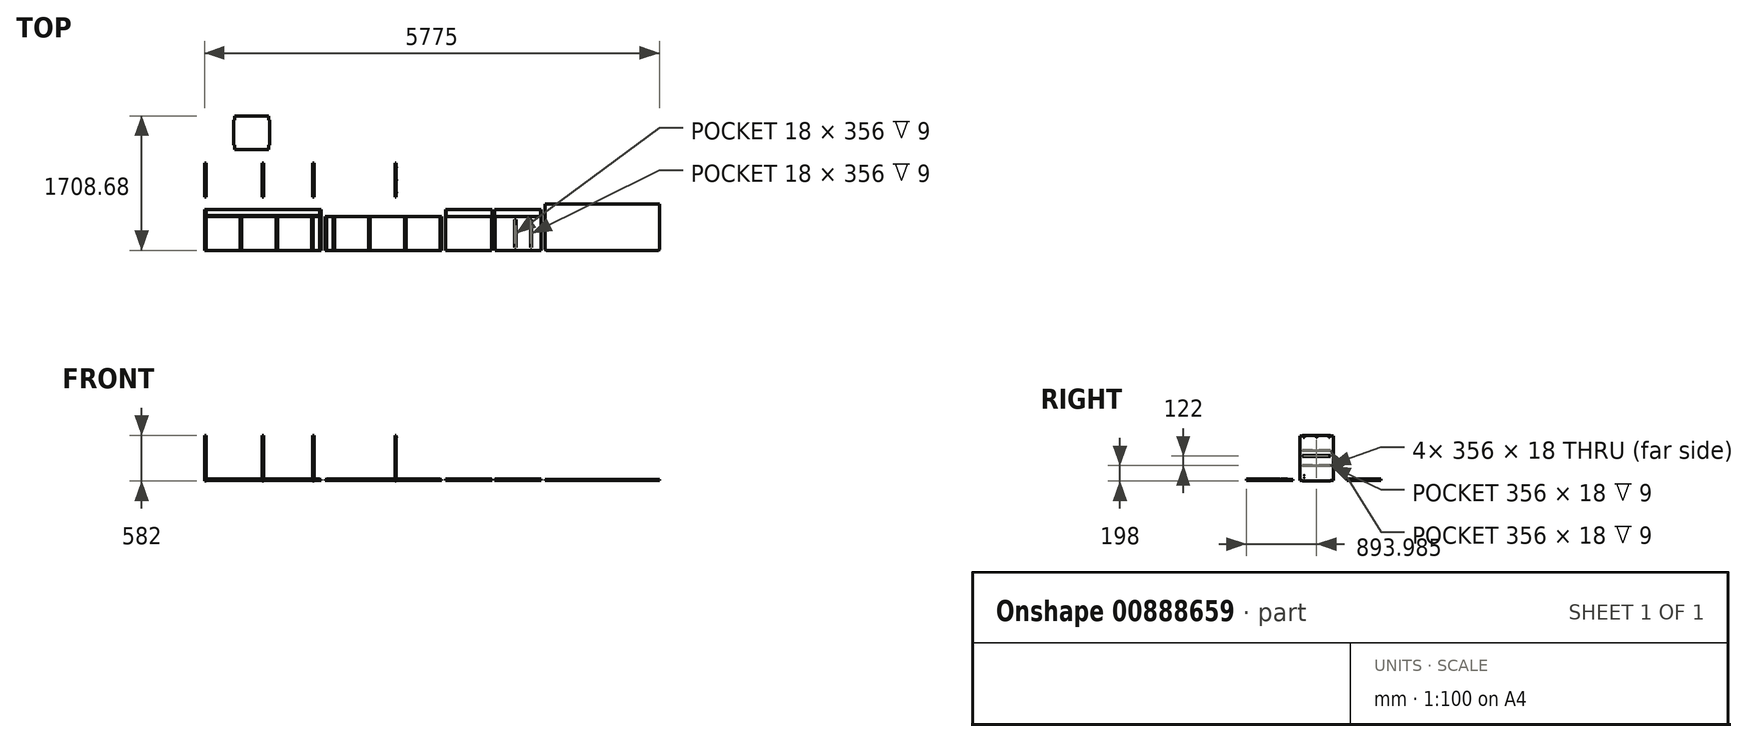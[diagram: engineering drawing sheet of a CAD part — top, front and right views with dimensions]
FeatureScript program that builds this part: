
annotation { "Feature Type Name" : "Feature", "Feature Type Description" : "" }
export const myFeature = defineFeature(function(context is Context, id is Id, definition is map)
    precondition{}
    {
        {
            assignVariable(context, id + "F0", {"name" : "ply", "anyValue" : 18});
        }
        {
            assignVariable(context, id + "F1", {"name" : "back_ply", "anyValue" : 12});
        }
        {
            assignVariable(context, id + "F2", {"name" : "cutter_rad", "anyValue" : 5});
        }
        {
            var Q0;
            Q0=qCreatedBy(makeId("Top.planeOp"),FACE);
            var sketch = newSketch(context, id + "F3", { "sketchPlane" : qUnion([Q0])});
            skLineSegment(sketch, "E0.bottom", {"start": v(0, 0) * mm, "end": v(1480, 0) * mm});
            skLineSegment(sketch, "E0.top", {"start": v(0, 520) * mm, "end": v(1480, 520) * mm});
            skLineSegment(sketch, "E0.left", {"start": v(0, 0) * mm, "end": v(0, 520) * mm});
            skLineSegment(sketch, "E0.right", {"start": v(1480, 0) * mm, "end": v(1480, 520) * mm});
            skSolve(sketch);
        }
        {
            var Q0;
            Q0=makeQuery(id+"F3.imprint","IMPRINT",FACE,{"disambiguationData":[TD([[makeQuery(id+"F3.imprint","IMPRINT",EDGE,{"derivedFrom":sQuery(id+"F3.wireOp",EDGE,"E0.bottom")}),1.0]])]});
            extrude(context, id + "F4", {"entities" : qUnion([Q0]), "depth" : (getVariable(context, 'ply')) * mm, "offsetDistance" : 25 * mm});
        }
        {
            var Q0;
            Q0=makeQuery(id+"F4.opExtrude","CAP_FACE",FACE,{"disambiguationData":[OSD([sQuery(id+"F3.wireOp",EDGE,"E0.bottom"),sQuery(id+"F3.wireOp",EDGE,"E0.top"),sQuery(id+"F3.wireOp",EDGE,"E0.left"),sQuery(id+"F3.wireOp",EDGE,"E0.right")])],"isStart":false});
            var sketch = newSketch(context, id + "F5", { "sketchPlane" : qUnion([Q0])});
            skLineSegment(sketch, "E1.bottom", {"start": v(14, 428) * mm, "end": v(1466, 428) * mm});
            skLineSegment(sketch, "E1.top", {"start": v(14, 440.5) * mm, "end": v(1466, 440.5) * mm});
            skLineSegment(sketch, "E1.left", {"start": v(9, 433) * mm, "end": v(9, 435.5) * mm});
            skLineSegment(sketch, "E1.right", {"start": v(1471, 433) * mm, "end": v(1471, 435.5) * mm});
            skPoint(sketch, "E2.visualSharp", {"position": v(9, 440.5) * mm});
            skArc(sketch, "E2.filletArc", {"start": v(14, 440.5) * mm, "mid": v(10.46, 439.04) * mm, "end": v(9, 435.5) * mm});
            skPoint(sketch, "E3.visualSharp", {"position": v(9, 428) * mm});
            skArc(sketch, "E3.filletArc", {"start": v(9, 433) * mm, "mid": v(10.46, 429.46) * mm, "end": v(14, 428) * mm});
            skPoint(sketch, "E4.visualSharp", {"position": v(1471, 440.5) * mm});
            skArc(sketch, "E4.filletArc", {"start": v(1471, 435.5) * mm, "mid": v(1469.54, 439.04) * mm, "end": v(1466, 440.5) * mm});
            skPoint(sketch, "E5.visualSharp", {"position": v(1471, 428) * mm});
            skArc(sketch, "E5.filletArc", {"start": v(1466, 428) * mm, "mid": v(1469.54, 429.46) * mm, "end": v(1471, 433) * mm});
            skLineSegment(sketch, "E6.bottom", {"start": v(0, 0) * mm, "end": v(18, 0) * mm});
            skLineSegment(sketch, "E6.top", {"start": v(0, 520) * mm, "end": v(18, 520) * mm});
            skLineSegment(sketch, "E6.left", {"start": v(0, 0) * mm, "end": v(0, 520) * mm});
            skLineSegment(sketch, "E6.right", {"start": v(18, 0) * mm, "end": v(18, 520) * mm});
            skLineSegment(sketch, "E7", {"start": v(740, 520) * mm, "end": v(740, 0) * mm, "construction": true});
            skLineSegment(sketch, "E8.MirrorCS", {"start": v(1462, 0) * mm, "end": v(1462, 520) * mm});
            skLineSegment(sketch, "E9.MirrorCS", {"start": v(1480, 520) * mm, "end": v(1462, 520) * mm});
            skLineSegment(sketch, "E10.MirrorCS", {"start": v(1480, 0) * mm, "end": v(1480, 520) * mm});
            skLineSegment(sketch, "E11.MirrorCS", {"start": v(1480, 0) * mm, "end": v(1462, 0) * mm});
            skLineSegment(sketch, "E12.bottom", {"start": v(458.33, 18) * mm, "end": v(466.33, 18) * mm});
            skLineSegment(sketch, "E12.top", {"start": v(458.33, 410) * mm, "end": v(466.33, 410) * mm});
            skLineSegment(sketch, "E12.left", {"start": v(453.33, 23) * mm, "end": v(453.33, 405) * mm});
            skLineSegment(sketch, "E12.right", {"start": v(471.33, 23) * mm, "end": v(471.33, 405) * mm});
            skPoint(sketch, "E13.visualSharp", {"position": v(453.33, 410) * mm});
            skArc(sketch, "E13.filletArc", {"start": v(458.33, 410) * mm, "mid": v(454.8, 408.54) * mm, "end": v(453.33, 405) * mm});
            skPoint(sketch, "E14.visualSharp", {"position": v(471.33, 410) * mm});
            skArc(sketch, "E14.filletArc", {"start": v(471.33, 405) * mm, "mid": v(469.87, 408.54) * mm, "end": v(466.33, 410) * mm});
            skPoint(sketch, "E15.visualSharp", {"position": v(453.33, 18) * mm});
            skArc(sketch, "E15.filletArc", {"start": v(453.33, 23) * mm, "mid": v(454.8, 19.46) * mm, "end": v(458.33, 18) * mm});
            skPoint(sketch, "E16.visualSharp", {"position": v(471.33, 18) * mm});
            skArc(sketch, "E16.filletArc", {"start": v(466.33, 18) * mm, "mid": v(469.87, 19.46) * mm, "end": v(471.33, 23) * mm});
            skLineSegment(sketch, "E17.bottom", {"start": v(911.67, 18) * mm, "end": v(919.67, 18) * mm});
            skLineSegment(sketch, "E17.top", {"start": v(911.67, 410) * mm, "end": v(919.67, 410) * mm});
            skLineSegment(sketch, "E17.left", {"start": v(906.67, 23) * mm, "end": v(906.67, 405) * mm});
            skLineSegment(sketch, "E17.right", {"start": v(924.67, 23) * mm, "end": v(924.67, 405) * mm});
            skPoint(sketch, "E18.visualSharp", {"position": v(906.67, 410) * mm});
            skArc(sketch, "E18.filletArc", {"start": v(911.67, 410) * mm, "mid": v(908.13, 408.54) * mm, "end": v(906.67, 405) * mm});
            skPoint(sketch, "E19.visualSharp", {"position": v(924.67, 410) * mm});
            skArc(sketch, "E19.filletArc", {"start": v(924.67, 405) * mm, "mid": v(923.2, 408.54) * mm, "end": v(919.67, 410) * mm});
            skPoint(sketch, "E20.visualSharp", {"position": v(906.67, 18) * mm});
            skArc(sketch, "E20.filletArc", {"start": v(906.67, 23) * mm, "mid": v(908.13, 19.46) * mm, "end": v(911.67, 18) * mm});
            skPoint(sketch, "E21.visualSharp", {"position": v(924.67, 18) * mm});
            skArc(sketch, "E21.filletArc", {"start": v(919.67, 18) * mm, "mid": v(923.2, 19.46) * mm, "end": v(924.67, 23) * mm});
            skLineSegment(sketch, "E22.bottom", {"start": v(1365, 18) * mm, "end": v(1373, 18) * mm});
            skLineSegment(sketch, "E22.top", {"start": v(1365, 410) * mm, "end": v(1373, 410) * mm});
            skLineSegment(sketch, "E22.left", {"start": v(1360, 23) * mm, "end": v(1360, 405) * mm});
            skLineSegment(sketch, "E22.right", {"start": v(1378, 23) * mm, "end": v(1378, 405) * mm});
            skPoint(sketch, "E23.visualSharp", {"position": v(1360, 410) * mm});
            skArc(sketch, "E23.filletArc", {"start": v(1365, 410) * mm, "mid": v(1361.46, 408.54) * mm, "end": v(1360, 405) * mm});
            skPoint(sketch, "E24.visualSharp", {"position": v(1378, 410) * mm});
            skArc(sketch, "E24.filletArc", {"start": v(1378, 405) * mm, "mid": v(1376.54, 408.54) * mm, "end": v(1373, 410) * mm});
            skPoint(sketch, "E25.visualSharp", {"position": v(1360, 18) * mm});
            skArc(sketch, "E25.filletArc", {"start": v(1360, 23) * mm, "mid": v(1361.46, 19.46) * mm, "end": v(1365, 18) * mm});
            skPoint(sketch, "E26.visualSharp", {"position": v(1378, 18) * mm});
            skArc(sketch, "E26.filletArc", {"start": v(1373, 18) * mm, "mid": v(1376.54, 19.46) * mm, "end": v(1378, 23) * mm});
            skSolve(sketch);
        }
        {
            var Q0;
            Q0 = qSketchRegion(id + "F5", true);
            extrude(context, id + "F6", {"entities" : qUnion([Q0]), "operationType" : NewBodyOperationType.REMOVE, "oppositeDirection" : true, "depth" : (getVariable(context, 'ply') / 2) * mm, "offsetDistance" : 25 * mm});
        }
        {
            var Q0;
            Q0=qCreatedBy(makeId("Top.planeOp"),FACE);
            var sketch = newSketch(context, id + "F7", { "sketchPlane" : qUnion([Q0])});
            skLineSegment(sketch, "E27.bottom", {"start": v(1530, 0) * mm, "end": v(3010, 0) * mm});
            skLineSegment(sketch, "E27.top", {"start": v(1530, 428) * mm, "end": v(3010, 428) * mm});
            skLineSegment(sketch, "E27.left", {"start": v(1530, 0) * mm, "end": v(1530, 428) * mm});
            skLineSegment(sketch, "E27.right", {"start": v(3010, 0) * mm, "end": v(3010, 428) * mm});
            skSolve(sketch);
        }
        {
            var Q0;
            Q0 = qSketchRegion(id + "F7", true);
            extrude(context, id + "F8", {"entities" : qUnion([Q0]), "depth" : (getVariable(context, 'ply')) * mm, "offsetDistance" : 25 * mm});
        }
        {
            var Q0;
            Q0=makeQuery(id+"F8.opExtrude","CAP_FACE",FACE,{"disambiguationData":[OSD([sQuery(id+"F7.wireOp",EDGE,"E27.bottom"),sQuery(id+"F7.wireOp",EDGE,"E27.top"),sQuery(id+"F7.wireOp",EDGE,"E27.left"),sQuery(id+"F7.wireOp",EDGE,"E27.right")])],"isStart":false});
            var sketch = newSketch(context, id + "F9", { "sketchPlane" : qUnion([Q0])});
            skLineSegment(sketch, "E28.bottom", {"start": v(1530, 0) * mm, "end": v(1548, 0) * mm});
            skLineSegment(sketch, "E28.top", {"start": v(1530, 428) * mm, "end": v(1548, 428) * mm});
            skLineSegment(sketch, "E28.left", {"start": v(1530, 0) * mm, "end": v(1530, 428) * mm});
            skLineSegment(sketch, "E28.right", {"start": v(1548, 0) * mm, "end": v(1548, 428) * mm});
            skLineSegment(sketch, "E29", {"start": v(2270, 493) * mm, "end": v(2270, 65) * mm, "construction": true});
            skLineSegment(sketch, "E30.MirrorCS", {"start": v(2992, 0) * mm, "end": v(2992, 428) * mm});
            skLineSegment(sketch, "E31.MirrorCS", {"start": v(3010, 0) * mm, "end": v(3010, 428) * mm});
            skLineSegment(sketch, "E32.MirrorCS", {"start": v(3010, 428) * mm, "end": v(2992, 428) * mm});
            skLineSegment(sketch, "E33.MirrorCS", {"start": v(3010, 0) * mm, "end": v(2992, 0) * mm});
            skLineSegment(sketch, "E34.bottom", {"start": v(1637, 18) * mm, "end": v(1645, 18) * mm});
            skLineSegment(sketch, "E34.top", {"start": v(1637, 410) * mm, "end": v(1645, 410) * mm});
            skLineSegment(sketch, "E34.left", {"start": v(1632, 23) * mm, "end": v(1632, 405) * mm});
            skLineSegment(sketch, "E34.right", {"start": v(1650, 23) * mm, "end": v(1650, 405) * mm});
            skPoint(sketch, "E35.visualSharp", {"position": v(1632, 410) * mm});
            skArc(sketch, "E35.filletArc", {"start": v(1637, 410) * mm, "mid": v(1633.46, 408.54) * mm, "end": v(1632, 405) * mm});
            skPoint(sketch, "E36.visualSharp", {"position": v(1650, 410) * mm});
            skArc(sketch, "E36.filletArc", {"start": v(1650, 405) * mm, "mid": v(1648.54, 408.54) * mm, "end": v(1645, 410) * mm});
            skPoint(sketch, "E37.visualSharp", {"position": v(1632, 18) * mm});
            skArc(sketch, "E37.filletArc", {"start": v(1632, 23) * mm, "mid": v(1633.46, 19.46) * mm, "end": v(1637, 18) * mm});
            skPoint(sketch, "E38.visualSharp", {"position": v(1650, 18) * mm});
            skArc(sketch, "E38.filletArc", {"start": v(1645, 18) * mm, "mid": v(1648.54, 19.46) * mm, "end": v(1650, 23) * mm});
            skLineSegment(sketch, "E39.bottom", {"start": v(2090.33, 18) * mm, "end": v(2098.33, 18) * mm});
            skLineSegment(sketch, "E39.top", {"start": v(2090.33, 410) * mm, "end": v(2098.33, 410) * mm});
            skLineSegment(sketch, "E39.left", {"start": v(2085.33, 23) * mm, "end": v(2085.33, 405) * mm});
            skLineSegment(sketch, "E39.right", {"start": v(2103.33, 23) * mm, "end": v(2103.33, 405) * mm});
            skPoint(sketch, "E40.visualSharp", {"position": v(2085.33, 410) * mm});
            skArc(sketch, "E40.filletArc", {"start": v(2090.33, 410) * mm, "mid": v(2086.8, 408.54) * mm, "end": v(2085.33, 405) * mm});
            skPoint(sketch, "E41.visualSharp", {"position": v(2103.33, 410) * mm});
            skArc(sketch, "E41.filletArc", {"start": v(2103.33, 405) * mm, "mid": v(2101.87, 408.54) * mm, "end": v(2098.33, 410) * mm});
            skPoint(sketch, "E42.visualSharp", {"position": v(2085.33, 18) * mm});
            skArc(sketch, "E42.filletArc", {"start": v(2085.33, 23) * mm, "mid": v(2086.8, 19.46) * mm, "end": v(2090.33, 18) * mm});
            skPoint(sketch, "E43.visualSharp", {"position": v(2103.33, 18) * mm});
            skArc(sketch, "E43.filletArc", {"start": v(2098.33, 18) * mm, "mid": v(2101.87, 19.46) * mm, "end": v(2103.33, 23) * mm});
            skLineSegment(sketch, "E44.bottom", {"start": v(2543.67, 18) * mm, "end": v(2551.67, 18) * mm});
            skLineSegment(sketch, "E44.top", {"start": v(2543.67, 410) * mm, "end": v(2551.67, 410) * mm});
            skLineSegment(sketch, "E44.left", {"start": v(2538.67, 23) * mm, "end": v(2538.67, 405) * mm});
            skLineSegment(sketch, "E44.right", {"start": v(2556.67, 23) * mm, "end": v(2556.67, 405) * mm});
            skPoint(sketch, "E45.visualSharp", {"position": v(2538.67, 410) * mm});
            skArc(sketch, "E45.filletArc", {"start": v(2543.67, 410) * mm, "mid": v(2540.13, 408.54) * mm, "end": v(2538.67, 405) * mm});
            skPoint(sketch, "E46.visualSharp", {"position": v(2556.67, 410) * mm});
            skArc(sketch, "E46.filletArc", {"start": v(2556.67, 405) * mm, "mid": v(2555.2, 408.54) * mm, "end": v(2551.67, 410) * mm});
            skPoint(sketch, "E47.visualSharp", {"position": v(2538.67, 18) * mm});
            skArc(sketch, "E47.filletArc", {"start": v(2538.67, 23) * mm, "mid": v(2540.13, 19.46) * mm, "end": v(2543.67, 18) * mm});
            skPoint(sketch, "E48.visualSharp", {"position": v(2556.67, 18) * mm});
            skArc(sketch, "E48.filletArc", {"start": v(2551.67, 18) * mm, "mid": v(2555.2, 19.46) * mm, "end": v(2556.67, 23) * mm});
            skSolve(sketch);
        }
        {
            var Q0;
            Q0=makeQuery(id+"F9.imprint","IMPRINT",FACE,{"disambiguationData":[TD([[makeQuery(id+"F9.imprint","IMPRINT",EDGE,{"derivedFrom":sQuery(id+"F9.wireOp",EDGE,"E28.bottom")}),1.0]])]});
            var Q1;
            Q1=makeQuery(id+"F9.imprint","IMPRINT",FACE,{"disambiguationData":[TD([[makeQuery(id+"F9.imprint","IMPRINT",EDGE,{"derivedFrom":sQuery(id+"F9.wireOp",EDGE,"E30.MirrorCS")}),-1.0]])]});
            var Q2;
            Q2=makeQuery(id+"F9.imprint","IMPRINT",FACE,{"disambiguationData":[TD([[makeQuery(id+"F9.imprint","IMPRINT",EDGE,{"derivedFrom":sQuery(id+"F9.wireOp",EDGE,"E34.bottom")}),1.0]])]});
            var Q3;
            Q3=makeQuery(id+"F9.imprint","IMPRINT",FACE,{"disambiguationData":[TD([[makeQuery(id+"F9.imprint","IMPRINT",EDGE,{"derivedFrom":sQuery(id+"F9.wireOp",EDGE,"E39.bottom")}),1.0]])]});
            var Q4;
            Q4=makeQuery(id+"F9.imprint","IMPRINT",FACE,{"disambiguationData":[TD([[makeQuery(id+"F9.imprint","IMPRINT",EDGE,{"derivedFrom":sQuery(id+"F9.wireOp",EDGE,"E44.bottom")}),1.0]])]});
            extrude(context, id + "F10", {"entities" : qUnion([Q0, Q1, Q2, Q3, Q4]), "operationType" : NewBodyOperationType.REMOVE, "oppositeDirection" : true, "depth" : (getVariable(context, 'ply') / 2) * mm, "offsetDistance" : 25 * mm});
        }
        {
            var Q0;
            Q0=qCreatedBy(makeId("Top.planeOp"),FACE);
            var sketch = newSketch(context, id + "F11", { "sketchPlane" : qUnion([Q0])});
            skLineSegment(sketch, "E49.bottom", {"start": v(3060, 0) * mm, "end": v(3642, 0) * mm});
            skLineSegment(sketch, "E49.top", {"start": v(3060, 520) * mm, "end": v(3642, 520) * mm});
            skLineSegment(sketch, "E49.left", {"start": v(3060, 0) * mm, "end": v(3060, 520) * mm});
            skLineSegment(sketch, "E49.right", {"start": v(3642, 0) * mm, "end": v(3642, 520) * mm});
            skSolve(sketch);
        }
        {
            var Q0;
            Q0=makeQuery(id+"F11.imprint","IMPRINT",FACE,{"disambiguationData":[TD([[makeQuery(id+"F11.imprint","IMPRINT",EDGE,{"derivedFrom":sQuery(id+"F11.wireOp",EDGE,"E49.bottom")}),1.0]])]});
            extrude(context, id + "F12", {"entities" : qUnion([Q0]), "depth" : (getVariable(context, 'ply')) * mm, "offsetDistance" : 25 * mm});
        }
        {
            var Q0;
            Q0=makeQuery(id+"F12.opExtrude","CAP_FACE",FACE,{"disambiguationData":[OSD([sQuery(id+"F11.wireOp",EDGE,"E49.bottom"),sQuery(id+"F11.wireOp",EDGE,"E49.top"),sQuery(id+"F11.wireOp",EDGE,"E49.left"),sQuery(id+"F11.wireOp",EDGE,"E49.right")])],"isStart":false});
            var sketch = newSketch(context, id + "F13", { "sketchPlane" : qUnion([Q0])});
            skLineSegment(sketch, "E50.bottom", {"start": v(3060, 520) * mm, "end": v(3642, 520) * mm});
            skLineSegment(sketch, "E50.top", {"start": v(3060, 428) * mm, "end": v(3642, 428) * mm});
            skLineSegment(sketch, "E50.left", {"start": v(3060, 520) * mm, "end": v(3060, 428) * mm});
            skLineSegment(sketch, "E50.right", {"start": v(3642, 520) * mm, "end": v(3642, 428) * mm});
            skSolve(sketch);
        }
        {
            var Q0;
            Q0 = qSketchRegion(id + "F13", true);
            extrude(context, id + "F14", {"entities" : qUnion([Q0]), "operationType" : NewBodyOperationType.REMOVE, "oppositeDirection" : true, "depth" : 4 * mm, "offsetDistance" : 25 * mm});
        }
        {
            var Q0;
            Q0=qCreatedBy(makeId("Top.planeOp"),FACE);
            var sketch = newSketch(context, id + "F15", { "sketchPlane" : qUnion([Q0])});
            skLineSegment(sketch, "E51.bottom", {"start": v(3692, 0) * mm, "end": v(4274, 0) * mm});
            skLineSegment(sketch, "E51.top", {"start": v(3692, 520) * mm, "end": v(4274, 520) * mm});
            skLineSegment(sketch, "E51.left", {"start": v(3692, 0) * mm, "end": v(3692, 520) * mm});
            skLineSegment(sketch, "E51.right", {"start": v(4274, 0) * mm, "end": v(4274, 520) * mm});
            skSolve(sketch);
        }
        {
            var Q0;
            Q0=makeQuery(id+"F15.imprint","IMPRINT",FACE,{"disambiguationData":[TD([[makeQuery(id+"F15.imprint","IMPRINT",EDGE,{"derivedFrom":sQuery(id+"F15.wireOp",EDGE,"E51.bottom")}),1.0]])]});
            extrude(context, id + "F16", {"entities" : qUnion([Q0]), "depth" : (getVariable(context, 'ply')) * mm, "offsetDistance" : 25 * mm});
        }
        {
            var Q0;
            Q0=makeQuery(id+"F16.opExtrude","CAP_FACE",FACE,{"disambiguationData":[OSD([sQuery(id+"F15.wireOp",EDGE,"E51.bottom"),sQuery(id+"F15.wireOp",EDGE,"E51.top"),sQuery(id+"F15.wireOp",EDGE,"E51.left"),sQuery(id+"F15.wireOp",EDGE,"E51.right")])],"isStart":false});
            var sketch = newSketch(context, id + "F17", { "sketchPlane" : qUnion([Q0])});
            skLineSegment(sketch, "E52.bottom", {"start": v(3692, 520) * mm, "end": v(4274, 520) * mm});
            skLineSegment(sketch, "E52.top", {"start": v(3692, 428) * mm, "end": v(4274, 428) * mm});
            skLineSegment(sketch, "E52.left", {"start": v(3692, 520) * mm, "end": v(3692, 428) * mm});
            skLineSegment(sketch, "E52.right", {"start": v(4274, 520) * mm, "end": v(4274, 428) * mm});
            skSolve(sketch);
        }
        {
            var Q0;
            Q0=makeQuery(id+"F17.imprint","IMPRINT",FACE,{"disambiguationData":[TD([[makeQuery(id+"F17.imprint","IMPRINT",EDGE,{"derivedFrom":sQuery(id+"F17.wireOp",EDGE,"E52.bottom")}),-1.0]])]});
            extrude(context, id + "F18", {"entities" : qUnion([Q0]), "operationType" : NewBodyOperationType.REMOVE, "oppositeDirection" : true, "depth" : 4 * mm, "offsetDistance" : 25 * mm});
        }
        {
            var Q0;
            Q0=makeQuery(id+"F16.opExtrude","SWEPT_FACE",FACE,{"disambiguationData":[OSD([sQuery(id+"F15.wireOp",EDGE,"E51.left")])]});
            var sketch = newSketch(context, id + "F19", { "sketchPlane" : qUnion([Q0])});
            skLineSegment(sketch, "E53.bottom", {"start": v(-520, 0) * mm, "end": v(-428, 0) * mm});
            skLineSegment(sketch, "E53.top", {"start": v(-520, 14) * mm, "end": v(-428, 14) * mm});
            skLineSegment(sketch, "E53.left", {"start": v(-520, 0) * mm, "end": v(-520, 14) * mm});
            skLineSegment(sketch, "E53.right", {"start": v(-428, 0) * mm, "end": v(-428, 14) * mm});
            skSolve(sketch);
        }
        {
            var Q0;
            Q0 = qSketchRegion(id + "F19", true);
            extrude(context, id + "F20", {"entities" : qUnion([Q0]), "operationType" : NewBodyOperationType.ADD, "depth" : (getVariable(context, 'ply') / 2) * mm, "offsetDistance" : 25 * mm});
        }
        {
            var Q0;
            Q0=makeQuery(id+"F12.opExtrude","SWEPT_FACE",FACE,{"disambiguationData":[OSD([sQuery(id+"F11.wireOp",EDGE,"E49.right")])]});
            var sketch = newSketch(context, id + "F21", { "sketchPlane" : qUnion([Q0])});
            skLineSegment(sketch, "E54.bottom", {"start": v(520, 0) * mm, "end": v(428, 0) * mm});
            skLineSegment(sketch, "E54.top", {"start": v(520, 14) * mm, "end": v(428, 14) * mm});
            skLineSegment(sketch, "E54.left", {"start": v(520, 0) * mm, "end": v(520, 14) * mm});
            skLineSegment(sketch, "E54.right", {"start": v(428, 0) * mm, "end": v(428, 14) * mm});
            skSolve(sketch);
        }
        {
            var Q0;
            Q0 = qSketchRegion(id + "F21", true);
            extrude(context, id + "F22", {"entities" : qUnion([Q0]), "operationType" : NewBodyOperationType.ADD, "depth" : (getVariable(context, 'ply') / 2) * mm, "offsetDistance" : 25 * mm});
        }
        {
            var Q0;
            Q0=makeQuery(id+"F22.boolean.opBoolean","MERGE",FACE,{"derivedFrom":[makeQuery(id+"F14.boolean.opBoolean","COPY",FACE,{"derivedFrom":makeQuery(id+"F14.opExtrude","CAP_FACE",FACE,{"disambiguationData":[OSD([sQuery(id+"F13.wireOp",EDGE,"E50.bottom"),sQuery(id+"F13.wireOp",EDGE,"E50.top"),sQuery(id+"F13.wireOp",EDGE,"E50.left"),sQuery(id+"F13.wireOp",EDGE,"E50.right")])],"isStart":false})}),makeQuery(id+"F22.opExtrude","SWEPT_FACE",FACE,{"disambiguationData":[OSD([sQuery(id+"F21.wireOp",EDGE,"E54.top")])]})]});
            var sketch = newSketch(context, id + "F23", { "sketchPlane" : qUnion([Q0])});
            skLineSegment(sketch, "E55.bottom", {"start": v(3060, 520) * mm, "end": v(3069, 520) * mm});
            skLineSegment(sketch, "E55.top", {"start": v(3060, 440.5) * mm, "end": v(3069, 440.5) * mm});
            skLineSegment(sketch, "E55.left", {"start": v(3060, 520) * mm, "end": v(3060, 440.5) * mm});
            skLineSegment(sketch, "E55.right", {"start": v(3069, 520) * mm, "end": v(3069, 440.5) * mm});
            skSolve(sketch);
        }
        {
            var Q0;
            Q0 = qSketchRegion(id + "F23", true);
            extrude(context, id + "F24", {"entities" : qUnion([Q0]), "operationType" : NewBodyOperationType.ADD, "depth" : 4 * mm, "offsetDistance" : 25 * mm});
        }
        {
            var Q0;
            Q0=makeQuery(id+"F20.boolean.opBoolean","MERGE",FACE,{"derivedFrom":[makeQuery(id+"F18.boolean.opBoolean","COPY",FACE,{"derivedFrom":makeQuery(id+"F18.opExtrude","CAP_FACE",FACE,{"disambiguationData":[OSD([sQuery(id+"F17.wireOp",EDGE,"E52.bottom"),sQuery(id+"F17.wireOp",EDGE,"E52.top"),sQuery(id+"F17.wireOp",EDGE,"E52.left"),sQuery(id+"F17.wireOp",EDGE,"E52.right")])],"isStart":false})}),makeQuery(id+"F20.opExtrude","SWEPT_FACE",FACE,{"disambiguationData":[OSD([sQuery(id+"F19.wireOp",EDGE,"E53.top")])]})]});
            var sketch = newSketch(context, id + "F25", { "sketchPlane" : qUnion([Q0])});
            skLineSegment(sketch, "E56.bottom", {"start": v(4274, 520) * mm, "end": v(4265, 520) * mm});
            skLineSegment(sketch, "E56.top", {"start": v(4274, 440.5) * mm, "end": v(4265, 440.5) * mm});
            skLineSegment(sketch, "E56.left", {"start": v(4274, 520) * mm, "end": v(4274, 440.5) * mm});
            skLineSegment(sketch, "E56.right", {"start": v(4265, 520) * mm, "end": v(4265, 440.5) * mm});
            skSolve(sketch);
        }
        {
            var Q0;
            Q0 = qSketchRegion(id + "F25", true);
            extrude(context, id + "F26", {"entities" : qUnion([Q0]), "operationType" : NewBodyOperationType.ADD, "depth" : 4 * mm, "offsetDistance" : 25 * mm});
        }
        {
            var Q0;
            Q0=qCreatedBy(makeId("Top.planeOp"),FACE);
            var sketch = newSketch(context, id + "F27", { "sketchPlane" : qUnion([Q0])});
            skLineSegment(sketch, "E57.bottom", {"start": v(4324, 0) * mm, "end": v(5775, 0) * mm});
            skLineSegment(sketch, "E57.top", {"start": v(4324, 590) * mm, "end": v(5775, 590) * mm});
            skLineSegment(sketch, "E57.left", {"start": v(4324, 0) * mm, "end": v(4324, 590) * mm});
            skLineSegment(sketch, "E57.right", {"start": v(5775, 0) * mm, "end": v(5775, 590) * mm});
            skLineSegment(sketch, "E58", {"start": v(4324, 10) * mm, "end": v(4334, 0) * mm});
            skLineSegment(sketch, "E59", {"start": v(5049.5, 590) * mm, "end": v(5049.5, 0) * mm, "construction": true});
            skLineSegment(sketch, "E60.MirrorCS", {"start": v(5775, 10) * mm, "end": v(5765, 0) * mm});
            skSolve(sketch);
        }
        {
            var Q0;
            {var subQ2=sQuery(id+"F27.wireOp",EDGE,"E57.top");Q0=makeQuery(id+"F27.imprint","IMPRINT",FACE,{"disambiguationData":[TD([[makeQuery(id+"F27.imprint","IMPRINT",EDGE,{"derivedFrom":subQ2}),-1.0]])]});}
            extrude(context, id + "F28", {"entities" : qUnion([Q0]), "depth" : (getVariable(context, 'back_ply')) * mm, "offsetDistance" : 25 * mm});
        }
        {
            var Q0;
            Q0=qCreatedBy(makeId("Right.planeOp"),FACE);
            var sketch = newSketch(context, id + "F29", { "sketchPlane" : qUnion([Q0])});
            skLineSegment(sketch, "E61.bottom", {"start": v(679.99, 0) * mm, "end": v(1107.99, 0) * mm});
            skLineSegment(sketch, "E61.top", {"start": v(679.99, 564) * mm, "end": v(1107.99, 564) * mm});
            skLineSegment(sketch, "E61.left", {"start": v(679.99, 0) * mm, "end": v(679.99, 564) * mm});
            skLineSegment(sketch, "E61.right", {"start": v(1107.99, 0) * mm, "end": v(1107.99, 564) * mm});
            skSolve(sketch);
        }
        {
            var Q0;
            Q0=makeQuery(id+"F29.imprint","IMPRINT",FACE,{"disambiguationData":[TD([[makeQuery(id+"F29.imprint","IMPRINT",EDGE,{"derivedFrom":sQuery(id+"F29.wireOp",EDGE,"E61.bottom")}),1.0]])]});
            extrude(context, id + "F30", {"entities" : qUnion([Q0]), "depth" : (getVariable(context, 'ply')) * mm, "offsetDistance" : 25 * mm});
        }
        {
            var Q0;
            Q0=makeQuery(id+"F30.opExtrude","SWEPT_FACE",FACE,{"disambiguationData":[OSD([sQuery(id+"F29.wireOp",EDGE,"E61.bottom")])]});
            var sketch = newSketch(context, id + "F31", { "sketchPlane" : qUnion([Q0])});
            skLineSegment(sketch, "E62.bottom", {"start": v(0, -715.99) * mm, "end": v(18, -715.99) * mm});
            skLineSegment(sketch, "E62.top", {"start": v(0, -1071.99) * mm, "end": v(18, -1071.99) * mm});
            skLineSegment(sketch, "E62.left", {"start": v(0, -715.99) * mm, "end": v(0, -1071.99) * mm});
            skLineSegment(sketch, "E62.right", {"start": v(18, -715.99) * mm, "end": v(18, -1071.99) * mm});
            skSolve(sketch);
        }
        {
            var Q0;
            Q0=makeQuery(id+"F31.imprint","IMPRINT",FACE,{"disambiguationData":[TD([[makeQuery(id+"F31.imprint","IMPRINT",EDGE,{"derivedFrom":sQuery(id+"F31.wireOp",EDGE,"E62.bottom")}),-1.0]])]});
            extrude(context, id + "F32", {"entities" : qUnion([Q0]), "operationType" : NewBodyOperationType.ADD, "depth" : (getVariable(context, 'ply') / 2) * mm, "offsetDistance" : 25 * mm});
        }
        {
            var Q0;
            Q0=makeQuery(id+"F30.opExtrude","SWEPT_FACE",FACE,{"disambiguationData":[OSD([sQuery(id+"F29.wireOp",EDGE,"E61.top")])]});
            var sketch = newSketch(context, id + "F33", { "sketchPlane" : qUnion([Q0])});
            skLineSegment(sketch, "E63.bottom", {"start": v(0, 1071.99) * mm, "end": v(18, 1071.99) * mm});
            skLineSegment(sketch, "E63.top", {"start": v(0, 715.99) * mm, "end": v(18, 715.99) * mm});
            skLineSegment(sketch, "E63.left", {"start": v(0, 1071.99) * mm, "end": v(0, 715.99) * mm});
            skLineSegment(sketch, "E63.right", {"start": v(18, 1071.99) * mm, "end": v(18, 715.99) * mm});
            skSolve(sketch);
        }
        {
            var Q0;
            Q0=makeQuery(id+"F33.imprint","IMPRINT",FACE,{"disambiguationData":[TD([[makeQuery(id+"F33.imprint","IMPRINT",EDGE,{"derivedFrom":sQuery(id+"F33.wireOp",EDGE,"E63.bottom")}),-1.0]])]});
            extrude(context, id + "F34", {"entities" : qUnion([Q0]), "operationType" : NewBodyOperationType.ADD, "depth" : (getVariable(context, 'ply') / 2) * mm, "offsetDistance" : 25 * mm});
        }
        {
            var Q0;
            Q0=makeQuery(id+"F30.opExtrude","SWEPT_BODY",BODY,{"disambiguationData":[OSD([sQuery(id+"F29.wireOp",EDGE,"E61.bottom"),sQuery(id+"F29.wireOp",EDGE,"E61.top"),sQuery(id+"F29.wireOp",EDGE,"E61.left"),sQuery(id+"F29.wireOp",EDGE,"E61.right")])]});
            transform(context, id + "F35", {"entities" : qUnion([Q0]), "transformType" : TransformType.TRANSLATION_3D, "dx" : 730 * mm, "dy" : 0 * mm, "dz" : 0 * mm, "makeCopy" : true});
        }
        {
            var Q0;
            Q0=makeQuery(id+"F30.opExtrude","SWEPT_BODY",BODY,{"disambiguationData":[OSD([sQuery(id+"F29.wireOp",EDGE,"E61.bottom"),sQuery(id+"F29.wireOp",EDGE,"E61.top"),sQuery(id+"F29.wireOp",EDGE,"E61.left"),sQuery(id+"F29.wireOp",EDGE,"E61.right")])]});
            transform(context, id + "F36", {"entities" : qUnion([Q0]), "transformType" : TransformType.TRANSLATION_3D, "dx" : 1370 * mm, "dy" : 0 * mm, "dz" : 0 * mm, "makeCopy" : true});
        }
        {
            var Q0;
            Q0=makeQuery(id+"F30.opExtrude","SWEPT_BODY",BODY,{"disambiguationData":[OSD([sQuery(id+"F29.wireOp",EDGE,"E61.bottom"),sQuery(id+"F29.wireOp",EDGE,"E61.top"),sQuery(id+"F29.wireOp",EDGE,"E61.left"),sQuery(id+"F29.wireOp",EDGE,"E61.right")])]});
            transform(context, id + "F37", {"entities" : qUnion([Q0]), "transformType" : TransformType.TRANSLATION_3D, "dx" : 2420 * mm, "dy" : 0 * mm, "dz" : 0 * mm, "makeCopy" : true});
        }
        {
            var Q0;
            Q0=makeQuery(id+"F35.opPattern","COPY",FACE,{"derivedFrom":makeQuery(id+"F34.boolean.opBoolean","MERGE",FACE,{"derivedFrom":[makeQuery(id+"F32.boolean.opBoolean","MERGE",FACE,{"derivedFrom":[makeQuery(id+"F30.opExtrude","CAP_FACE",FACE,{"disambiguationData":[OSD([sQuery(id+"F29.wireOp",EDGE,"E61.bottom"),sQuery(id+"F29.wireOp",EDGE,"E61.top"),sQuery(id+"F29.wireOp",EDGE,"E61.left"),sQuery(id+"F29.wireOp",EDGE,"E61.right")])],"isStart":false}),makeQuery(id+"F32.opExtrude","SWEPT_FACE",FACE,{"disambiguationData":[OSD([sQuery(id+"F31.wireOp",EDGE,"E62.right")])]})]}),makeQuery(id+"F34.opExtrude","SWEPT_FACE",FACE,{"disambiguationData":[OSD([sQuery(id+"F33.wireOp",EDGE,"E63.right")])]})]}),"instanceName":"1"});
            var sketch = newSketch(context, id + "F38", { "sketchPlane" : qUnion([Q0])});
            skLineSegment(sketch, "E64.bottom", {"start": v(715.99, 384) * mm, "end": v(1071.99, 384) * mm});
            skLineSegment(sketch, "E64.top", {"start": v(715.99, 366) * mm, "end": v(1071.99, 366) * mm});
            skLineSegment(sketch, "E64.left", {"start": v(715.99, 384) * mm, "end": v(715.99, 366) * mm});
            skLineSegment(sketch, "E64.right", {"start": v(1071.99, 384) * mm, "end": v(1071.99, 366) * mm});
            skLineSegment(sketch, "E65.bottom", {"start": v(715.99, 198) * mm, "end": v(1071.99, 198) * mm});
            skLineSegment(sketch, "E65.top", {"start": v(715.99, 180) * mm, "end": v(1071.99, 180) * mm});
            skLineSegment(sketch, "E65.left", {"start": v(715.99, 198) * mm, "end": v(715.99, 180) * mm});
            skLineSegment(sketch, "E65.right", {"start": v(1071.99, 198) * mm, "end": v(1071.99, 180) * mm});
            skSolve(sketch);
        }
        {
            var Q0;
            Q0=makeQuery(id+"F38.imprint","IMPRINT",FACE,{"disambiguationData":[TD([[makeQuery(id+"F38.imprint","IMPRINT",EDGE,{"derivedFrom":sQuery(id+"F38.wireOp",EDGE,"E64.bottom")}),-1.0]])]});
            var Q1;
            Q1=makeQuery(id+"F38.imprint","IMPRINT",FACE,{"disambiguationData":[TD([[makeQuery(id+"F38.imprint","IMPRINT",EDGE,{"derivedFrom":sQuery(id+"F38.wireOp",EDGE,"E65.bottom")}),-1.0]])]});
            extrude(context, id + "F39", {"entities" : qUnion([Q0, Q1]), "operationType" : NewBodyOperationType.REMOVE, "oppositeDirection" : true, "depth" : (getVariable(context, 'ply') / 2) * mm, "offsetDistance" : 25 * mm});
        }
        {
            var Q0;
            Q0=makeQuery(id+"F36.opPattern","COPY",FACE,{"derivedFrom":makeQuery(id+"F34.boolean.opBoolean","MERGE",FACE,{"derivedFrom":[makeQuery(id+"F32.boolean.opBoolean","MERGE",FACE,{"derivedFrom":[makeQuery(id+"F30.opExtrude","CAP_FACE",FACE,{"disambiguationData":[OSD([sQuery(id+"F29.wireOp",EDGE,"E61.bottom"),sQuery(id+"F29.wireOp",EDGE,"E61.top"),sQuery(id+"F29.wireOp",EDGE,"E61.left"),sQuery(id+"F29.wireOp",EDGE,"E61.right")])],"isStart":true}),makeQuery(id+"F32.opExtrude","SWEPT_FACE",FACE,{"disambiguationData":[OSD([sQuery(id+"F31.wireOp",EDGE,"E62.left")])]})]}),makeQuery(id+"F34.opExtrude","SWEPT_FACE",FACE,{"disambiguationData":[OSD([sQuery(id+"F33.wireOp",EDGE,"E63.left")])]})]}),"instanceName":"1"});
            var sketch = newSketch(context, id + "F40", { "sketchPlane" : qUnion([Q0])});
            skLineSegment(sketch, "E66.bottom", {"start": v(-1071.99, 384) * mm, "end": v(-715.99, 384) * mm});
            skLineSegment(sketch, "E66.top", {"start": v(-1071.99, 366) * mm, "end": v(-715.99, 366) * mm});
            skLineSegment(sketch, "E66.left", {"start": v(-1071.99, 384) * mm, "end": v(-1071.99, 366) * mm});
            skLineSegment(sketch, "E66.right", {"start": v(-715.99, 384) * mm, "end": v(-715.99, 366) * mm});
            skLineSegment(sketch, "E67.bottom", {"start": v(-1071.99, 198) * mm, "end": v(-715.99, 198) * mm});
            skLineSegment(sketch, "E67.top", {"start": v(-1071.99, 180) * mm, "end": v(-715.99, 180) * mm});
            skLineSegment(sketch, "E67.left", {"start": v(-1071.99, 198) * mm, "end": v(-1071.99, 180) * mm});
            skLineSegment(sketch, "E67.right", {"start": v(-715.99, 198) * mm, "end": v(-715.99, 180) * mm});
            skLineSegment(sketch, "E68.bottom", {"start": v(-1071.99, 320) * mm, "end": v(-715.99, 320) * mm});
            skLineSegment(sketch, "E68.top", {"start": v(-1071.99, 302) * mm, "end": v(-715.99, 302) * mm});
            skLineSegment(sketch, "E68.left", {"start": v(-1071.99, 320) * mm, "end": v(-1071.99, 302) * mm});
            skLineSegment(sketch, "E68.right", {"start": v(-715.99, 320) * mm, "end": v(-715.99, 302) * mm});
            skSolve(sketch);
        }
        {
            var Q0;
            Q0=makeQuery(id+"F40.imprint","IMPRINT",FACE,{"disambiguationData":[TD([[makeQuery(id+"F40.imprint","IMPRINT",EDGE,{"derivedFrom":sQuery(id+"F40.wireOp",EDGE,"E66.bottom")}),-1.0]])]});
            var Q1;
            Q1=makeQuery(id+"F40.imprint","IMPRINT",FACE,{"disambiguationData":[TD([[makeQuery(id+"F40.imprint","IMPRINT",EDGE,{"derivedFrom":sQuery(id+"F40.wireOp",EDGE,"E67.bottom")}),-1.0]])]});
            extrude(context, id + "F41", {"entities" : qUnion([Q0, Q1]), "operationType" : NewBodyOperationType.REMOVE, "oppositeDirection" : true, "depth" : (getVariable(context, 'ply') / 2) * mm, "offsetDistance" : 25 * mm});
        }
        {
            var Q0;
            Q0=makeQuery(id+"F40.imprint","IMPRINT",FACE,{"disambiguationData":[TD([[makeQuery(id+"F40.imprint","IMPRINT",EDGE,{"derivedFrom":sQuery(id+"F40.wireOp",EDGE,"E68.bottom")}),-1.0]])]});
            extrude(context, id + "F42", {"entities" : qUnion([Q0]), "operationType" : NewBodyOperationType.REMOVE, "oppositeDirection" : true, "depth" : (getVariable(context, 'ply')) * mm, "offsetDistance" : 25 * mm});
        }
        {
            var Q0;
            Q0=makeQuery(id+"F37.opPattern","COPY",FACE,{"derivedFrom":makeQuery(id+"F34.boolean.opBoolean","MERGE",FACE,{"derivedFrom":[makeQuery(id+"F32.boolean.opBoolean","MERGE",FACE,{"derivedFrom":[makeQuery(id+"F30.opExtrude","CAP_FACE",FACE,{"disambiguationData":[OSD([sQuery(id+"F29.wireOp",EDGE,"E61.bottom"),sQuery(id+"F29.wireOp",EDGE,"E61.top"),sQuery(id+"F29.wireOp",EDGE,"E61.left"),sQuery(id+"F29.wireOp",EDGE,"E61.right")])],"isStart":false}),makeQuery(id+"F32.opExtrude","SWEPT_FACE",FACE,{"disambiguationData":[OSD([sQuery(id+"F31.wireOp",EDGE,"E62.right")])]})]}),makeQuery(id+"F34.opExtrude","SWEPT_FACE",FACE,{"disambiguationData":[OSD([sQuery(id+"F33.wireOp",EDGE,"E63.right")])]})]}),"instanceName":"1"});
            var sketch = newSketch(context, id + "F43", { "sketchPlane" : qUnion([Q0])});
            skLineSegment(sketch, "E69.bottom", {"start": v(715.99, 320) * mm, "end": v(1071.99, 320) * mm});
            skLineSegment(sketch, "E69.top", {"start": v(715.99, 302) * mm, "end": v(1071.99, 302) * mm});
            skLineSegment(sketch, "E69.left", {"start": v(715.99, 320) * mm, "end": v(715.99, 302) * mm});
            skLineSegment(sketch, "E69.right", {"start": v(1071.99, 320) * mm, "end": v(1071.99, 302) * mm});
            skLineSegment(sketch, "E70.bottom", {"start": v(715.99, 256) * mm, "end": v(1071.99, 256) * mm});
            skLineSegment(sketch, "E70.top", {"start": v(715.99, 238) * mm, "end": v(1071.99, 238) * mm});
            skLineSegment(sketch, "E70.left", {"start": v(715.99, 256) * mm, "end": v(715.99, 238) * mm});
            skLineSegment(sketch, "E70.right", {"start": v(1071.99, 256) * mm, "end": v(1071.99, 238) * mm});
            skLineSegment(sketch, "E71.bottom", {"start": v(715.99, 454) * mm, "end": v(1071.99, 454) * mm});
            skLineSegment(sketch, "E71.top", {"start": v(715.99, 436) * mm, "end": v(1071.99, 436) * mm});
            skLineSegment(sketch, "E71.left", {"start": v(715.99, 454) * mm, "end": v(715.99, 436) * mm});
            skLineSegment(sketch, "E71.right", {"start": v(1071.99, 454) * mm, "end": v(1071.99, 436) * mm});
            skCircle(sketch, "E72", {"center": v(737.99, 206) * mm, "radius": 1 * mm});
            skCircle(sketch, "E73", {"center": v(737.99, 174) * mm, "radius": 1 * mm});
            skLineSegment(sketch, "E74", {"start": v(737.99, 206) * mm, "end": v(737.99, 174) * mm, "construction": true});
            skLineSegment(sketch, "E75", {"start": v(737.99, 190) * mm, "end": v(609.37, 190) * mm, "construction": true});
            skLineSegment(sketch, "E76", {"start": v(609.37, 119) * mm, "end": v(737.99, 119) * mm, "construction": true});
            skCircle(sketch, "E77.MirrorC", {"center": v(737.99, 32) * mm, "radius": 1 * mm});
            skCircle(sketch, "E78.MirrorC", {"center": v(737.99, 64) * mm, "radius": 1 * mm});
            skLineSegment(sketch, "E79", {"start": v(737.99, 64) * mm, "end": v(737.99, 32) * mm, "construction": true});
            skCircle(sketch, "E80", {"center": v(733.99, 550) * mm, "radius": 5 * mm});
            skCircle(sketch, "E81", {"center": v(893.99, 550) * mm, "radius": 5 * mm});
            skCircle(sketch, "E82", {"center": v(1053.99, 550) * mm, "radius": 5 * mm});
            skSolve(sketch);
        }
        {
            var Q0;
            Q0=makeQuery(id+"F43.imprint","IMPRINT",FACE,{"disambiguationData":[TD([[makeQuery(id+"F43.imprint","IMPRINT",EDGE,{"derivedFrom":sQuery(id+"F43.wireOp",EDGE,"E69.bottom")}),-1.0]])]});
            extrude(context, id + "F44", {"entities" : qUnion([Q0]), "operationType" : NewBodyOperationType.REMOVE, "oppositeDirection" : true, "depth" : (getVariable(context, 'ply')) * mm, "offsetDistance" : 25 * mm});
        }
        {
            var Q0;
            Q0=makeQuery(id+"F43.imprint","IMPRINT",FACE,{"disambiguationData":[TD([[makeQuery(id+"F43.imprint","IMPRINT",EDGE,{"derivedFrom":sQuery(id+"F43.wireOp",EDGE,"E71.bottom")}),-1.0]])]});
            var Q1;
            Q1=makeQuery(id+"F43.imprint","IMPRINT",FACE,{"disambiguationData":[TD([[makeQuery(id+"F43.imprint","IMPRINT",EDGE,{"derivedFrom":sQuery(id+"F43.wireOp",EDGE,"E70.bottom")}),-1.0]])]});
            var Q2;
            Q2=makeQuery(id+"F43.imprint","IMPRINT",FACE,{"disambiguationData":[TD([[makeQuery(id+"F43.imprint","IMPRINT",EDGE,{"derivedFrom":sQuery(id+"F43.wireOp",EDGE,"E72")}),1.0]])]});
            var Q3;
            Q3=makeQuery(id+"F43.imprint","IMPRINT",FACE,{"disambiguationData":[TD([[makeQuery(id+"F43.imprint","IMPRINT",EDGE,{"derivedFrom":sQuery(id+"F43.wireOp",EDGE,"E73")}),1.0]])]});
            var Q4;
            Q4=makeQuery(id+"F43.imprint","IMPRINT",FACE,{"disambiguationData":[TD([[makeQuery(id+"F43.imprint","IMPRINT",EDGE,{"derivedFrom":sQuery(id+"F43.wireOp",EDGE,"E78.MirrorC")}),-1.0]])]});
            var Q5;
            Q5=makeQuery(id+"F43.imprint","IMPRINT",FACE,{"disambiguationData":[TD([[makeQuery(id+"F43.imprint","IMPRINT",EDGE,{"derivedFrom":sQuery(id+"F43.wireOp",EDGE,"E77.MirrorC")}),-1.0]])]});
            extrude(context, id + "F45", {"entities" : qUnion([Q0, Q1, Q2, Q3, Q4, Q5]), "operationType" : NewBodyOperationType.REMOVE, "oppositeDirection" : true, "depth" : (getVariable(context, 'ply') / 2) * mm, "offsetDistance" : 25 * mm});
        }
        {
            var Q0;
            Q0=makeQuery(id+"F16.opExtrude","CAP_FACE",FACE,{"disambiguationData":[OSD([sQuery(id+"F15.wireOp",EDGE,"E51.bottom"),sQuery(id+"F15.wireOp",EDGE,"E51.top"),sQuery(id+"F15.wireOp",EDGE,"E51.left"),sQuery(id+"F15.wireOp",EDGE,"E51.right")])],"isStart":false});
            var sketch = newSketch(context, id + "F46", { "sketchPlane" : qUnion([Q0])});
            skLineSegment(sketch, "E83.bottom", {"start": v(4155, 392) * mm, "end": v(4137, 392) * mm});
            skLineSegment(sketch, "E83.top", {"start": v(4155, 36) * mm, "end": v(4137, 36) * mm});
            skLineSegment(sketch, "E83.left", {"start": v(4155, 392) * mm, "end": v(4155, 36) * mm});
            skLineSegment(sketch, "E83.right", {"start": v(4137, 392) * mm, "end": v(4137, 36) * mm});
            skLineSegment(sketch, "E84.bottom", {"start": v(3957, 392) * mm, "end": v(3939, 392) * mm});
            skLineSegment(sketch, "E84.top", {"start": v(3957, 36) * mm, "end": v(3939, 36) * mm});
            skLineSegment(sketch, "E84.left", {"start": v(3957, 392) * mm, "end": v(3957, 36) * mm});
            skLineSegment(sketch, "E84.right", {"start": v(3939, 392) * mm, "end": v(3939, 36) * mm});
            skSolve(sketch);
        }
        {
            var Q0;
            Q0=makeQuery(id+"F46.imprint","IMPRINT",FACE,{"disambiguationData":[TD([[makeQuery(id+"F46.imprint","IMPRINT",EDGE,{"derivedFrom":sQuery(id+"F46.wireOp",EDGE,"E83.bottom")}),1.0]])]});
            var Q1;
            Q1=makeQuery(id+"F46.imprint","IMPRINT",FACE,{"disambiguationData":[TD([[makeQuery(id+"F46.imprint","IMPRINT",EDGE,{"derivedFrom":sQuery(id+"F46.wireOp",EDGE,"E84.bottom")}),1.0]])]});
            extrude(context, id + "F47", {"entities" : qUnion([Q0, Q1]), "operationType" : NewBodyOperationType.REMOVE, "oppositeDirection" : true, "depth" : (getVariable(context, 'ply') / 2) * mm, "offsetDistance" : 25 * mm});
        }
        {
            var Q0;
            Q0=qCreatedBy(makeId("Top.planeOp"),FACE);
            var sketch = newSketch(context, id + "F48", { "sketchPlane" : qUnion([Q0])});
            skLineSegment(sketch, "E85.bottom", {"start": v(379.79, 1280.68) * mm, "end": v(815.12, 1280.68) * mm});
            skLineSegment(sketch, "E85.top", {"start": v(379.79, 1708.68) * mm, "end": v(815.12, 1708.68) * mm});
            skLineSegment(sketch, "E85.left", {"start": v(379.79, 1280.68) * mm, "end": v(379.79, 1708.68) * mm});
            skLineSegment(sketch, "E85.right", {"start": v(815.12, 1280.68) * mm, "end": v(815.12, 1708.68) * mm});
            skSolve(sketch);
        }
        {
            var Q0;
            Q0=makeQuery(id+"F48.imprint","IMPRINT",FACE,{"disambiguationData":[TD([[makeQuery(id+"F48.imprint","IMPRINT",EDGE,{"derivedFrom":sQuery(id+"F48.wireOp",EDGE,"E85.bottom")}),1.0]])]});
            extrude(context, id + "F49", {"entities" : qUnion([Q0]), "depth" : (getVariable(context, 'ply')) * mm, "offsetDistance" : 25 * mm});
        }
        {
            var Q0;
            Q0=makeQuery(id+"F49.opExtrude","SWEPT_FACE",FACE,{"disambiguationData":[OSD([sQuery(id+"F48.wireOp",EDGE,"E85.right")])]});
            var sketch = newSketch(context, id + "F50", { "sketchPlane" : qUnion([Q0])});
            skLineSegment(sketch, "E86.bottom", {"start": v(1334.68, 0) * mm, "end": v(1654.68, 0) * mm});
            skLineSegment(sketch, "E86.top", {"start": v(1334.68, 18) * mm, "end": v(1654.68, 18) * mm});
            skLineSegment(sketch, "E86.left", {"start": v(1334.68, 0) * mm, "end": v(1334.68, 18) * mm});
            skLineSegment(sketch, "E86.right", {"start": v(1654.68, 0) * mm, "end": v(1654.68, 18) * mm});
            skSolve(sketch);
        }
        {
            var Q0;
            Q0=makeQuery(id+"F50.imprint","IMPRINT",FACE,{"disambiguationData":[TD([[makeQuery(id+"F50.imprint","IMPRINT",EDGE,{"derivedFrom":sQuery(id+"F50.wireOp",EDGE,"E86.bottom")}),1.0]])]});
            extrude(context, id + "F51", {"entities" : qUnion([Q0]), "operationType" : NewBodyOperationType.ADD, "depth" : (getVariable(context, 'ply') / 2) * mm, "offsetDistance" : 25 * mm});
        }
        {
            var Q0;
            Q0=makeQuery(id+"F49.opExtrude","SWEPT_FACE",FACE,{"disambiguationData":[OSD([sQuery(id+"F48.wireOp",EDGE,"E85.left")])]});
            var sketch = newSketch(context, id + "F52", { "sketchPlane" : qUnion([Q0])});
            skLineSegment(sketch, "E87.bottom", {"start": v(-1654.68, 0) * mm, "end": v(-1334.68, 0) * mm});
            skLineSegment(sketch, "E87.top", {"start": v(-1654.68, 18) * mm, "end": v(-1334.68, 18) * mm});
            skLineSegment(sketch, "E87.left", {"start": v(-1654.68, 0) * mm, "end": v(-1654.68, 18) * mm});
            skLineSegment(sketch, "E87.right", {"start": v(-1334.68, 0) * mm, "end": v(-1334.68, 18) * mm});
            skSolve(sketch);
        }
        {
            var Q0;
            Q0=makeQuery(id+"F52.imprint","IMPRINT",FACE,{"disambiguationData":[TD([[makeQuery(id+"F52.imprint","IMPRINT",EDGE,{"derivedFrom":sQuery(id+"F52.wireOp",EDGE,"E87.bottom")}),-1.0]])]});
            extrude(context, id + "F53", {"entities" : qUnion([Q0]), "operationType" : NewBodyOperationType.ADD, "depth" : (getVariable(context, 'ply') / 2) * mm, "offsetDistance" : 25 * mm});
        }
        {
            var Q0;
            Q0=makeQuery(id+"F32.opExtrude","CAP_EDGE",EDGE,{"disambiguationData":[OSD([sQuery(id+"F31.wireOp",EDGE,"E62.bottom")])],"isStart":true});
            var Q1;
            Q1=makeQuery(id+"F32.opExtrude","CAP_EDGE",EDGE,{"disambiguationData":[OSD([sQuery(id+"F31.wireOp",EDGE,"E62.top")])],"isStart":true});
            var Q2;
            Q2=makeQuery(id+"F34.opExtrude","CAP_EDGE",EDGE,{"disambiguationData":[OSD([sQuery(id+"F33.wireOp",EDGE,"E63.top")])],"isStart":true});
            var Q3;
            Q3=makeQuery(id+"F34.opExtrude","CAP_EDGE",EDGE,{"disambiguationData":[OSD([sQuery(id+"F33.wireOp",EDGE,"E63.bottom")])],"isStart":true});
            var Q4;
            Q4=makeQuery(id+"F22.opExtrude","CAP_EDGE",EDGE,{"disambiguationData":[OSD([sQuery(id+"F21.wireOp",EDGE,"E54.right")])],"isStart":true});
            var Q5;
            Q5=makeQuery(id+"F20.opExtrude","CAP_EDGE",EDGE,{"disambiguationData":[OSD([sQuery(id+"F19.wireOp",EDGE,"E53.right")])],"isStart":true});
            var Q6;
            Q6=makeQuery(id+"F53.opExtrude","CAP_EDGE",EDGE,{"disambiguationData":[OSD([sQuery(id+"F52.wireOp",EDGE,"E87.right")])],"isStart":true});
            var Q7;
            Q7=makeQuery(id+"F53.opExtrude","CAP_EDGE",EDGE,{"disambiguationData":[OSD([sQuery(id+"F52.wireOp",EDGE,"E87.left")])],"isStart":true});
            var Q8;
            Q8=makeQuery(id+"F51.opExtrude","CAP_EDGE",EDGE,{"disambiguationData":[OSD([sQuery(id+"F50.wireOp",EDGE,"E86.right")])],"isStart":true});
            var Q9;
            Q9=makeQuery(id+"F51.opExtrude","CAP_EDGE",EDGE,{"disambiguationData":[OSD([sQuery(id+"F50.wireOp",EDGE,"E86.left")])],"isStart":true});
            fillet(context, id + "F54", {"entities" : qUnion([Q0, Q1, Q2, Q3, Q4, Q5, Q6, Q7, Q8, Q9]), "radius" : (getVariable(context, 'cutter_rad')) * mm, "tangentPropagation" : true, "allowEdgeOverflow" : false});
        }
    });
